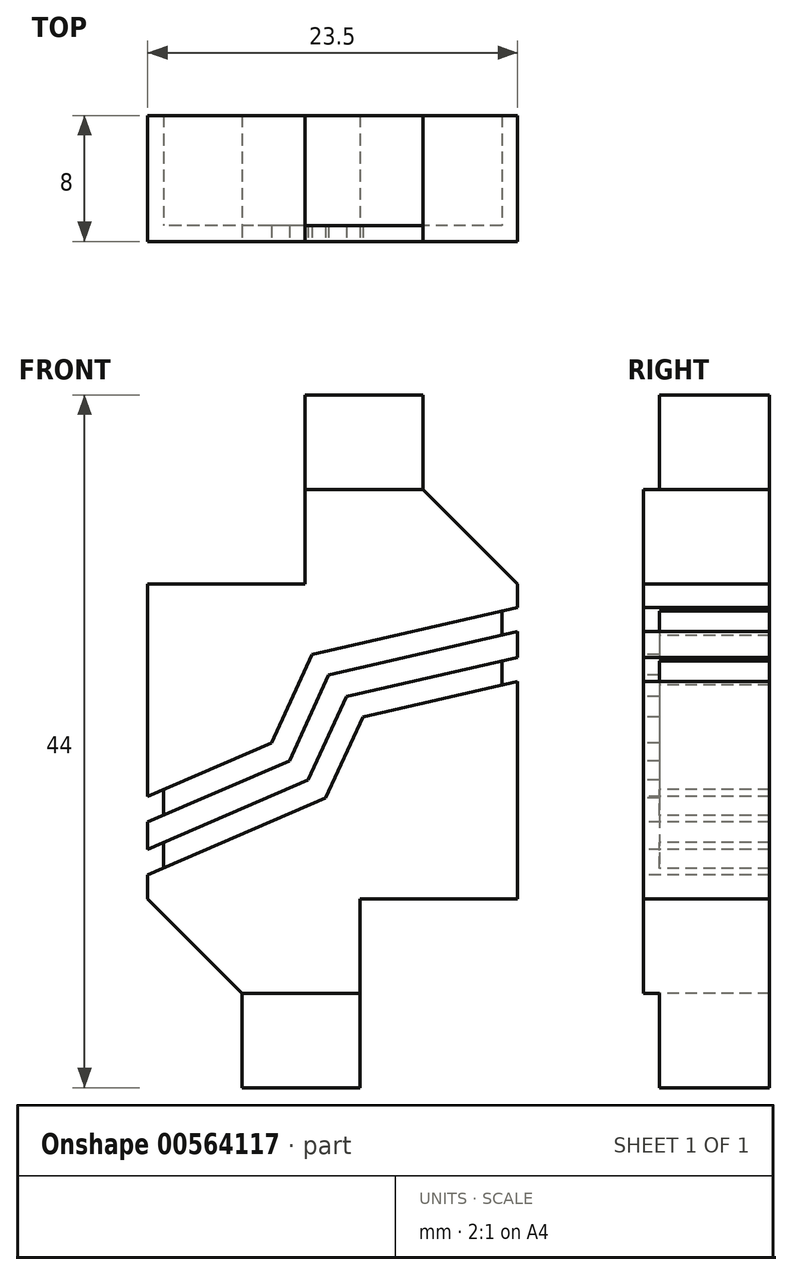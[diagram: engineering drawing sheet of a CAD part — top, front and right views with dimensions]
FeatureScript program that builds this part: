
annotation { "Feature Type Name" : "Feature", "Feature Type Description" : "" }
export const myFeature = defineFeature(function(context is Context, id is Id, definition is map)
    precondition{}
    {
        {
            var Q0;
            Q0=qCreatedBy(makeId("Front.planeOp"),FACE);
            var sketch = newSketch(context, id + "F0", { "sketchPlane" : qUnion([Q0])});
            skLineSegment(sketch, "E0.bottom", {"start": v(11.75, -22) * mm, "end": v(-11.75, -22) * mm});
            skLineSegment(sketch, "E0.top", {"start": v(11.75, 22) * mm, "end": v(-11.75, 22) * mm});
            skLineSegment(sketch, "E0.left", {"start": v(11.75, -22) * mm, "end": v(11.75, 22) * mm});
            skLineSegment(sketch, "E0.right", {"start": v(-11.75, -22) * mm, "end": v(-11.75, 22) * mm});
            skPoint(sketch, "E0.middle", {"position": v(0, 0) * mm});
            skSolve(sketch);
        }
        {
            var Q0;
            Q0 = qSketchRegion(id + "F0", true);
            extrude(context, id + "F1", {"entities" : qUnion([Q0]), "depth" : 8 * mm, "offsetDistance" : 25 * mm});
        }
        {
            var Q0;
            Q0=makeQuery(id+"F1.opExtrude","CAP_FACE",FACE,{"disambiguationData":[OSD([sQuery(id+"F0.wireOp",EDGE,"E0.bottom"),sQuery(id+"F0.wireOp",EDGE,"E0.top"),sQuery(id+"F0.wireOp",EDGE,"E0.left"),sQuery(id+"F0.wireOp",EDGE,"E0.right")])],"isStart":false});
            var sketch = newSketch(context, id + "F2", { "sketchPlane" : qUnion([Q0])});
            skLineSegment(sketch, "E1.bottom", {"start": v(-11.75, 22) * mm, "end": v(-1.75, 22) * mm});
            skLineSegment(sketch, "E1.top", {"start": v(-11.75, 10) * mm, "end": v(-1.75, 10) * mm});
            skLineSegment(sketch, "E1.left", {"start": v(-11.75, 22) * mm, "end": v(-11.75, 10) * mm});
            skLineSegment(sketch, "E1.right", {"start": v(-1.75, 22) * mm, "end": v(-1.75, 10) * mm});
            skLineSegment(sketch, "E2.bottom", {"start": v(11.75, -22) * mm, "end": v(1.75, -22) * mm});
            skLineSegment(sketch, "E2.top", {"start": v(11.75, -10) * mm, "end": v(1.75, -10) * mm});
            skLineSegment(sketch, "E2.left", {"start": v(11.75, -22) * mm, "end": v(11.75, -10) * mm});
            skLineSegment(sketch, "E2.right", {"start": v(1.75, -22) * mm, "end": v(1.75, -10) * mm});
            skLineSegment(sketch, "E3.bottom", {"start": v(11.75, 22) * mm, "end": v(5.75, 22) * mm});
            skLineSegment(sketch, "E3.left", {"start": v(11.75, 22) * mm, "end": v(11.75, 16) * mm});
            skLineSegment(sketch, "E3.right", {"start": v(5.75, 22) * mm, "end": v(5.75, 16) * mm});
            skLineSegment(sketch, "E4.bottom", {"start": v(-11.75, -22) * mm, "end": v(-5.75, -22) * mm});
            skLineSegment(sketch, "E4.left", {"start": v(-11.75, -22) * mm, "end": v(-11.75, -16) * mm});
            skLineSegment(sketch, "E4.right", {"start": v(-5.75, -22) * mm, "end": v(-5.75, -16) * mm});
            skLineSegment(sketch, "E5", {"start": v(11.75, 10) * mm, "end": v(5.75, 16) * mm});
            skLineSegment(sketch, "E6", {"start": v(11.75, 10) * mm, "end": v(11.75, 16) * mm});
            skLineSegment(sketch, "E7", {"start": v(-11.75, -10) * mm, "end": v(-5.75, -16) * mm});
            skLineSegment(sketch, "E8", {"start": v(-11.75, -10) * mm, "end": v(-11.75, -16) * mm});
            skSolve(sketch);
        }
        {
            var Q0;
            Q0 = qSketchRegion(id + "F2", true);
            extrude(context, id + "F3", {"entities" : qUnion([Q0]), "operationType" : NewBodyOperationType.REMOVE, "endBound" : BoundingType.UP_TO_NEXT, "oppositeDirection" : true, "depth" : 25 * mm, "offsetDistance" : 25 * mm});
        }
        {
            var Q0;
            Q0=makeQuery(id+"F1.opExtrude","CAP_FACE",FACE,{"disambiguationData":[OSD([sQuery(id+"F0.wireOp",EDGE,"E0.bottom"),sQuery(id+"F0.wireOp",EDGE,"E0.top"),sQuery(id+"F0.wireOp",EDGE,"E0.left"),sQuery(id+"F0.wireOp",EDGE,"E0.right")])],"isStart":false});
            var sketch = newSketch(context, id + "F4", { "sketchPlane" : qUnion([Q0])});
            skLineSegment(sketch, "E9", {"start": v(11.75, 6.96) * mm, "end": v(-0.25, 4.22) * mm});
            skLineSegment(sketch, "E10", {"start": v(-0.25, 4.22) * mm, "end": v(-2.75, -1.24) * mm});
            skLineSegment(sketch, "E11", {"start": v(-2.75, -1.24) * mm, "end": v(-11.75, -5.13) * mm});
            skLineSegment(sketch, "E12.0", {"start": v(-3.87, -0.1) * mm, "end": v(-11.75, -3.5) * mm});
            skLineSegment(sketch, "E12.1", {"start": v(-1.3, 5.51) * mm, "end": v(-3.87, -0.1) * mm});
            skLineSegment(sketch, "E12.2", {"start": v(11.75, 8.5) * mm, "end": v(-1.3, 5.51) * mm});
            skLineSegment(sketch, "E13.0", {"start": v(-1.56, -2.45) * mm, "end": v(-11.75, -6.87) * mm});
            skLineSegment(sketch, "E13.1", {"start": v(0.87, 2.84) * mm, "end": v(-1.56, -2.45) * mm});
            skLineSegment(sketch, "E13.2", {"start": v(11.75, 5.33) * mm, "end": v(0.87, 2.84) * mm});
            skLineSegment(sketch, "E14.0", {"start": v(-0.44, -3.6) * mm, "end": v(-11.75, -8.5) * mm});
            skLineSegment(sketch, "E14.1", {"start": v(1.92, 1.54) * mm, "end": v(-0.44, -3.6) * mm});
            skLineSegment(sketch, "E14.2", {"start": v(11.75, 3.8) * mm, "end": v(1.92, 1.54) * mm});
            skLineSegment(sketch, "E15", {"start": v(11.75, 8.5) * mm, "end": v(11.75, 6.96) * mm});
            skLineSegment(sketch, "E16", {"start": v(11.75, 5.33) * mm, "end": v(11.75, 3.8) * mm});
            skLineSegment(sketch, "E17", {"start": v(-11.75, -3.5) * mm, "end": v(-11.75, -5.13) * mm});
            skLineSegment(sketch, "E18", {"start": v(-11.75, -6.87) * mm, "end": v(-11.75, -8.5) * mm});
            skLineSegment(sketch, "E19.bottom", {"start": v(-1.75, 22) * mm, "end": v(5.75, 22) * mm});
            skLineSegment(sketch, "E19.top", {"start": v(-1.75, 16) * mm, "end": v(5.75, 16) * mm});
            skLineSegment(sketch, "E19.left", {"start": v(-1.75, 22) * mm, "end": v(-1.75, 16) * mm});
            skLineSegment(sketch, "E19.right", {"start": v(5.75, 22) * mm, "end": v(5.75, 16) * mm});
            skLineSegment(sketch, "E20.bottom", {"start": v(1.75, -22) * mm, "end": v(-5.75, -22) * mm});
            skLineSegment(sketch, "E20.top", {"start": v(1.75, -16) * mm, "end": v(-5.75, -16) * mm});
            skLineSegment(sketch, "E20.left", {"start": v(1.75, -22) * mm, "end": v(1.75, -16) * mm});
            skLineSegment(sketch, "E20.right", {"start": v(-5.75, -22) * mm, "end": v(-5.75, -16) * mm});
            skSolve(sketch);
        }
        {
            var Q0;
            Q0 = qSketchRegion(id + "F4", true);
            extrude(context, id + "F5", {"entities" : qUnion([Q0]), "operationType" : NewBodyOperationType.REMOVE, "oppositeDirection" : true, "depth" : 1 * mm, "offsetDistance" : 25 * mm});
        }
        {
            var Q0;
            Q0=makeQuery(id+"F5.boolean.opBoolean","COPY",FACE,{"derivedFrom":makeQuery(id+"F5.opExtrude","CAP_FACE",FACE,{"disambiguationData":[OSD([sQuery(id+"F4.wireOp",EDGE,"E9"),sQuery(id+"F4.wireOp",EDGE,"E10"),sQuery(id+"F4.wireOp",EDGE,"E11"),sQuery(id+"F4.wireOp",EDGE,"E12.0"),sQuery(id+"F4.wireOp",EDGE,"E12.1"),sQuery(id+"F4.wireOp",EDGE,"E12.2"),sQuery(id+"F4.wireOp",EDGE,"E15"),sQuery(id+"F4.wireOp",EDGE,"E17")])],"isStart":false})});
            var sketch = newSketch(context, id + "F6", { "sketchPlane" : qUnion([Q0])});
            skLineSegment(sketch, "E21.left", {"start": v(11.75, 8.5) * mm, "end": v(11.75, 6.96) * mm});
            skLineSegment(sketch, "E21.right", {"start": v(10.75, 8.27) * mm, "end": v(10.75, 6.73) * mm});
            skLineSegment(sketch, "E22.0", {"start": v(11.75, 8.5) * mm, "end": v(10.75, 8.27) * mm});
            skLineSegment(sketch, "E22.1", {"start": v(11.75, 6.96) * mm, "end": v(10.75, 6.73) * mm});
            skPoint(sketch, "E23.orphan", {"position": v(-1.3, 5.51) * mm});
            skPoint(sketch, "E24.orphan", {"position": v(-0.25, 4.22) * mm});
            skPoint(sketch, "E25.0", {"position": v(11.75, 5.33) * mm});
            skPoint(sketch, "E25.1", {"position": v(11.75, 3.8) * mm});
            skLineSegment(sketch, "E26.left", {"start": v(11.75, 5.33) * mm, "end": v(11.75, 3.8) * mm});
            skLineSegment(sketch, "E26.right", {"start": v(10.75, 5.1) * mm, "end": v(10.75, 3.56) * mm});
            skLineSegment(sketch, "E27", {"start": v(11.75, 5.33) * mm, "end": v(10.75, 5.1) * mm});
            skLineSegment(sketch, "E28", {"start": v(11.75, 3.8) * mm, "end": v(10.75, 3.56) * mm});
            skLineSegment(sketch, "E29.left", {"start": v(-11.75, -5.13) * mm, "end": v(-11.75, -3.5) * mm});
            skLineSegment(sketch, "E29.right", {"start": v(-10.75, -4.7) * mm, "end": v(-10.75, -3.07) * mm});
            skLineSegment(sketch, "E30", {"start": v(-10.75, -3.07) * mm, "end": v(-11.75, -3.5) * mm});
            skLineSegment(sketch, "E31", {"start": v(-11.75, -5.13) * mm, "end": v(-10.75, -4.7) * mm});
            skPoint(sketch, "E32.0", {"position": v(-11.75, -6.87) * mm});
            skPoint(sketch, "E32.1", {"position": v(-11.75, -8.5) * mm});
            skLineSegment(sketch, "E33.left", {"start": v(-11.75, -8.5) * mm, "end": v(-11.75, -6.87) * mm});
            skLineSegment(sketch, "E33.right", {"start": v(-10.75, -8.07) * mm, "end": v(-10.75, -6.43) * mm});
            skLineSegment(sketch, "E34", {"start": v(-11.75, -6.87) * mm, "end": v(-10.75, -6.43) * mm});
            skLineSegment(sketch, "E35", {"start": v(-11.75, -8.5) * mm, "end": v(-10.75, -8.07) * mm});
            skSolve(sketch);
        }
        {
            var Q0;
            Q0 = qSketchRegion(id + "F6", true);
            extrude(context, id + "F7", {"entities" : qUnion([Q0]), "operationType" : NewBodyOperationType.REMOVE, "endBound" : BoundingType.UP_TO_NEXT, "oppositeDirection" : true, "depth" : 25 * mm, "offsetDistance" : 25 * mm});
        }
    });
